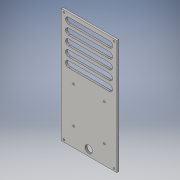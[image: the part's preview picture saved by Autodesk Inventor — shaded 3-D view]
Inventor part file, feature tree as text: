
AUTODESK INVENTOR PART (.ipt)
format: ipt  version: 2016 (Build 200138000, 138)  size: 152,576 bytes
history: native  units: mm
features: hole x3, sketch x3, extrude x2, mirror x2, pattern_linear x1
ambient origin geometry x8: Origin, YZ Plane, XZ Plane, XY Plane, X Axis, Y Axis, Z Axis, Center Point
bodies: Volumenkörper1 (feature_tree)
feature tree (11):
  extrude  "Extrusion1"  Depth=182.4mm
  hole  "Bohrung1"  [1 undecoded]
  extrude  "Extrusion2"  Depth=30.0mm
  pattern_linear  "Rechteckige Anordnung1"  Spacing1=75.0mm  [1 undecoded]
  hole  "Bohrung2"  [1 undecoded]
  mirror  "Spiegeln1"
  mirror  "Spiegeln2"
  hole  "Bohrung3"  [1 undecoded]
  sketch  "Skizze1"  dims[d0=88.6mm d1=182.4mm]
  sketch  "Skizze2"  dims[d2=3.0mm d3=0.0mm d5=49.0mm]
  sketch  "Skizze3"  dims[d6=58.0mm d7=30.0mm d8=3.0mm d9=6.0mm d10=4.0mm d11=2.0mm d12=90.0deg d13=2.5mm d14=0.0mm d15=75.0mm d16=10.0mm d18=5.0mm d19=5.0mm d20=5.0mm d21=10.0mm d22=0.0mm d23=50.0mm d25=15.0mm d26=4.4mm d27=3.4mm d28=3.0mm d29=6.0mm d30=4.0mm d31=2.0mm d32=90.0deg d33=8.0mm d34=20.594885mm d35=10.0mm d36=44.0mm d37=11.8mm d38=6.0mm d39=4.0mm d40=2.0mm d41=90.0deg d42=8.0mm d43=20.594885mm]
note: 4 required parameter values undecoded (feature->parameter linkage not recoverable at this tier; creation-order binding heuristic only, values carry confidence <= 0.55)
